# Revit family: Bath-Drop_In-Kohler-Hourglass-K_1219
name_source: partatom
category: Plumbing Fixtures
revit_build: Autodesk Revit 2015 (Build: 20140606_1530(x64)
units: mm (PartAtom-declared; Revit-internal decimal feet)

## types (3) — shared parameters
ADA Compliant = No
Assembly Code = D2010510
CW Connection = No
Default Elevation = 0' - 0"
Drain Diameter = 0' - 1 1/2"
Finish = Acrylic - Kohler - 0 - White
HW Connection = No
Height = 1' - 8"
Keynote = 22 40 00.D2
Length = 5' - 0"
Manufacturer = Kohler
Material = Acrylic
Product Documentation Link = http://www.us.kohler.com
Product Name = Hourglass 60'' x 32'' Drop-In Bath
Product Page URL = http://www.us.kohler.com
Sanitary Connector = Sanitary Drain
URL = http://www.us.kohler.com
Vent Connection = Yes
Version = 2014 - v1.0a
Waste Connection = Yes
Water Capacity = 64 gal (234.4 L)
Weight = 80 lbs (36.3 kg)
Width = 2' - 8"
zero-valued in all types: CWFU, HWFU, WFU

## per-type parameters (varying)
| type | ControlM | Description | Model |
| 0-White | 0 | 60'' x 32'' Drop-in Bath, White | K-1219-0 |
| 47-Almond | 47 | 60'' x 32'' Drop-in Bath, Almond | K-1219-47 |
| 96-Biscuit | 96 | 60'' x 32'' Drop-in Bath, Biscuit | K-1219-96 |

## geometry (parser evidence)
native form markers: Sweep x2
no freeform markers — native parametric forms only
